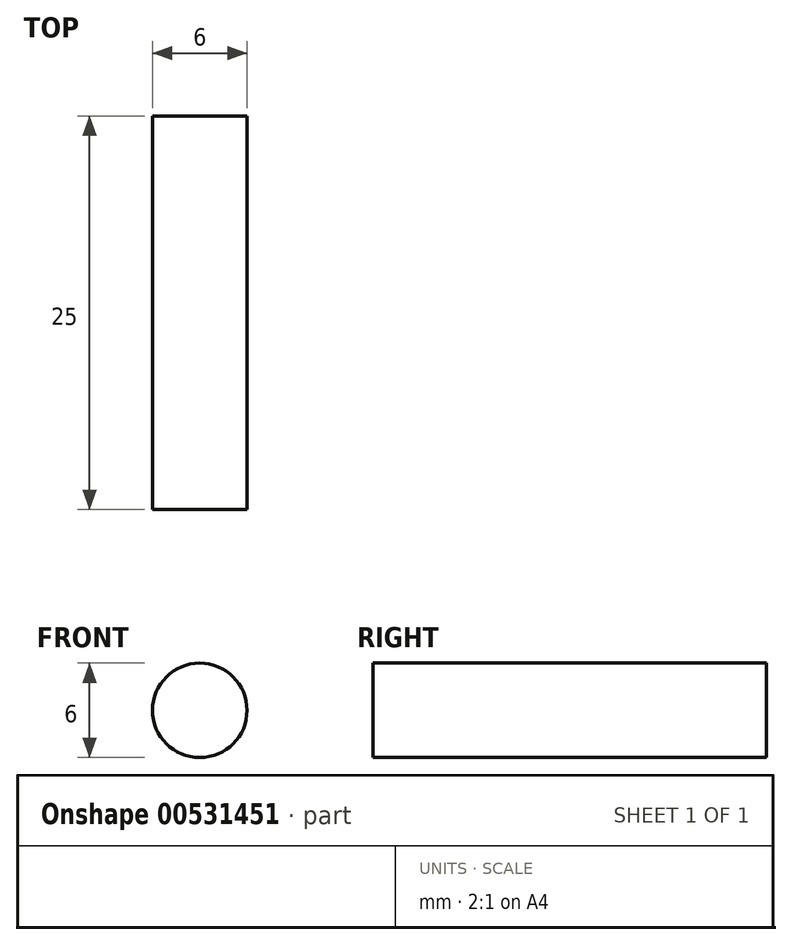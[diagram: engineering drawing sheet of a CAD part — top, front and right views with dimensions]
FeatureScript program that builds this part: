
annotation { "Feature Type Name" : "Feature", "Feature Type Description" : "" }
export const myFeature = defineFeature(function(context is Context, id is Id, definition is map)
    precondition{}
    {
        {
            var Q0;
            Q0=qCreatedBy(makeId("Front.planeOp"),FACE);
            var sketch = newSketch(context, id + "F0", { "sketchPlane" : qUnion([Q0])});
            skCircle(sketch, "E0", {"center": v(0, 0) * mm, "radius": 3 * mm});
            skSolve(sketch);
        }
        {
            var Q0;
            Q0 = qSketchRegion(id + "F0", true);
            extrude(context, id + "F1", {"entities" : qUnion([Q0]), "depth" : 25 * mm, "offsetDistance" : 25 * mm});
        }
    });
